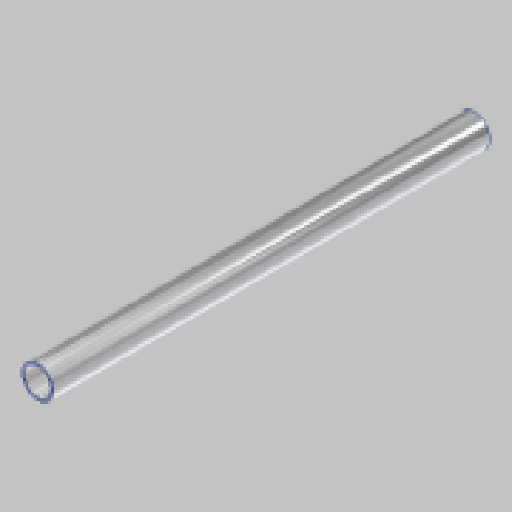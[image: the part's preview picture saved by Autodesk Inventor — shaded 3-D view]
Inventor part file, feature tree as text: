
AUTODESK INVENTOR PART (.ipt)
format: ipt  version: 2023.5 (Build 275446000, 446)  size: 241,664 bytes
history: native  units: in
note: dims shown in document units (in); Inventor stores cm internally (conversion verified against a paired STEP export)
features: extrude x1, sketch x1
ambient origin geometry x8: Origin, YZ Plane, XZ Plane, XY Plane, X Axis, Y Axis, Z Axis, Center Point
bodies: Solid1 (feature_tree)
feature tree (2):
  extrude  "Extrusion1"  Depth=12.0in
  sketch  "Sketch1"  dims[d0=0.875in d1=0.0625in d2=12.0in d3=0.0in]
